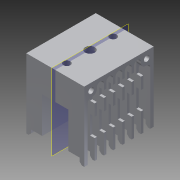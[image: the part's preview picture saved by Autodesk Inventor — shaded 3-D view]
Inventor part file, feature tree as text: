
AUTODESK INVENTOR PART (.ipt)
format: ipt  version: 2014 (Build 180170000, 170)  size: 556,032 bytes
history: native  units: mm
features: extrude x10, sketch x9, projected_geometry x7, thread x2, plane x2, mirror x2, reference x2, chamfer x1, fillet x1
ambient origin geometry x8: Origin, YZ Plane, XZ Plane, XY Plane, X Axis, Y Axis, Z Axis, Center Point
bodies: Solid1 (feature_tree)
feature tree (36):
  extrude  "Extrusion1"  Depth=7.0mm
  extrude  "Extrusion2"  Depth=30.0mm TaperAngle=0.0deg
  extrude  "Extrusion4"  Depth=1.5mm TaperAngle=0.0deg
  extrude  "Extrusion5"  Depth=3.0mm
  thread  "Thread1"  [1 undecoded]
  thread  "Thread2"  [1 undecoded]
  extrude  "Extrusion6"  Depth=3.0mm
  extrude  "Extrusion7"  Depth=3.0mm
  plane  "Work Plane1"
  extrude  "Extrusion9"  Depth=3.0mm
  mirror  "Mirror1"
  chamfer  "Chamfer1"  Distance=7.0mm
  fillet  "Fillet1"  Radius=10.0mm
  extrude  "Extrusion11"  Depth=10.0mm TaperAngle=0.0deg
  extrude  "Extrusion12"  Depth=1.5mm
  mirror  "Mirror2"
  sketch  "Sketch13"  dims[d23=3.0mm d24=7.0mm d25=0.0mm d26=10.0mm d27=0.0mm d28=10.0mm d29=0.0mm d34=1.5mm d35=4.0mm d37=1.5mm d38=3.0mm d39=3.0mm d40=3.0mm d41=3.0mm d42=3.0mm d43=1.5mm d44=1.0mm d45=1.0mm d46=1.0mm d47=1.0mm d48=3.0mm d49=3.0mm d51=1.0mm d52=6.0mm d53=0.0mm d57=2.0mm d58=2.5mm d59=0.0mm d65=2.0mm d66=0.0mm d73=1.0mm d74=2.0mm d75=45.0deg d76=2.0mm d77=8.0mm d78=5.0mm d79=3.0mm d80=4.0mm d81=0.0mm d82=2.0mm d83=0.0mm d84=0.15mm d85=0.15mm d86=10.0mm d87=0.0mm]
  plane  "Work Plane2"
  extrude  "Extrusion13"  Depth=4.0mm
  sketch  "Sketch1"  dims[d0=12.0mm d1=0.0mm d2=7.0mm]
  reference  "Reference1"
  sketch  "Sketch2"  dims[d3=7.0mm d4=30.0mm d5=0.0mm]
  sketch  "Sketch4"  dims[d9=4.1mm d10=1.5mm d11=0.0mm]
  sketch  "Sketch5"  dims[d12=3.0mm d13=2.4mm d14=3.0mm d15=2.4mm]
  sketch  "Sketch6"  dims[d16=3.0mm d17=3.0mm]
  sketch  "Sketch9"  dims[d18=3.0mm d19=3.0mm]
  sketch  "Sketch11"  dims[d20=3.0mm d21=3.0mm]
  projected_geometry  "Projected Loop1"
  projected_geometry  "Projected Loop2"
  projected_geometry  "Projected Loop3"
  sketch  "Sketch12"  dims[d22=3.0mm]
  projected_geometry  "Projected Loop4"
  projected_geometry  "Projected Loop5"
  projected_geometry  "Projected Loop6"
  projected_geometry  "Projected Loop7"
  reference  "Reference3"
note: 2 required parameter values undecoded (feature->parameter linkage not recoverable at this tier; creation-order binding heuristic only, values carry confidence <= 0.55)
